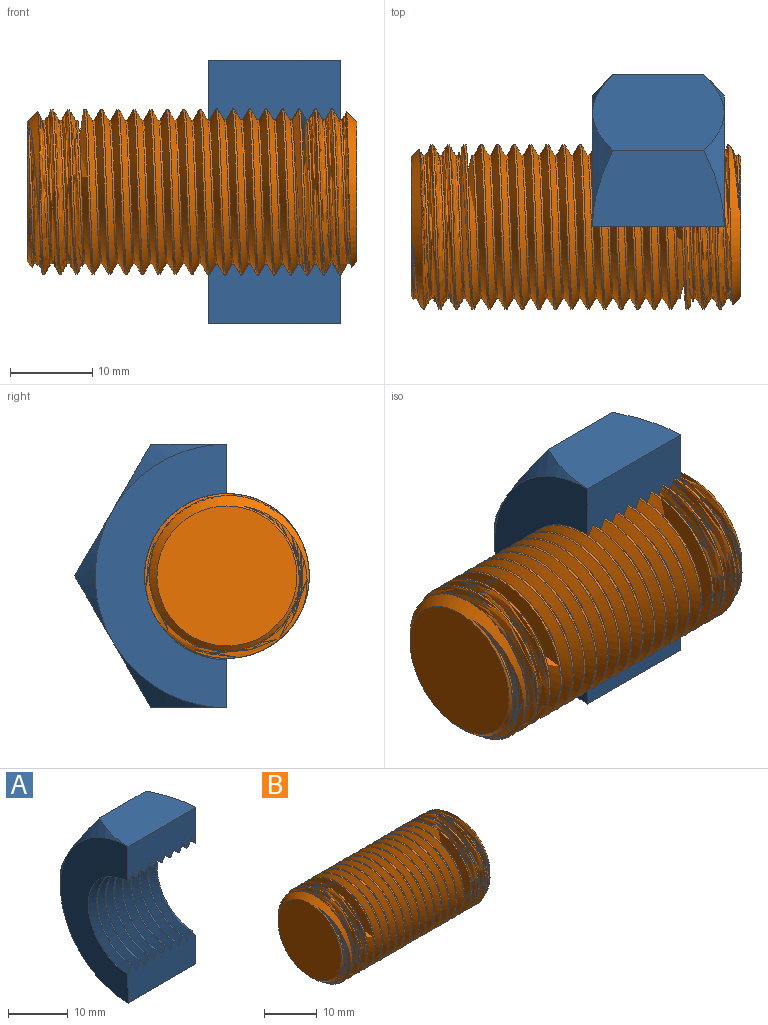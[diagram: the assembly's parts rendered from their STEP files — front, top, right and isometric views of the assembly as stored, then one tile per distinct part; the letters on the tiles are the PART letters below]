
ASSEMBLY  parts=2 mates=1
PART A: 49 faces, bbox 18.7x28.2x37.9 mm
  f0: plane 16x7.23mm, normal (0,-1,0), area 105.3mm2, adj f9,f11,f12,f13,f14,f15,f16,f17
  f1: cone r=18.5mm half-angle=45deg, axis (-1,0,0), area 19.5mm2, adj f2,f4,f47
  f2: plane 16.01x16mm, normal (0,0.87,-0.5), area 264.2mm2, adj f1,f3,f4,f6,f7,f8
  f3: cone r=18.5mm half-angle=45deg, axis (-1,0,0), area 19.5mm2, adj f2,f6,f47
  f4: plane 16.01x16mm, normal (0,0.87,0.5), area 264.2mm2, adj f1,f2,f5,f8,f9,f10
  f5: cone r=18.5mm half-angle=45deg, axis (-1,0,0), area 19.5mm2, adj f4,f9,f47
  f6: plane 16.01x9.24mm, normal (0,0,-1), area 132.1mm2, adj f2,f3,f7,f48
  f7: cone r=18.5mm half-angle=45deg, axis (1,0,0), area 19.5mm2, adj f2,f6,f46
  f8: cone r=18.5mm half-angle=45deg, axis (1,0,0), area 19.5mm2, adj f2,f4,f46
  f9: plane 16.01x9.24mm, normal (0,0,1), area 132.1mm2, adj f0,f4,f5,f10
  f10: cone r=18.5mm half-angle=45deg, axis (1,0,0), area 19.5mm2, adj f4,f9,f46
  f11: cylinder r=8.77mm len=17.53mm, axis (-1,0,0), area 7.2mm2, adj f0,f12,f19,f48
  f12: bspline ~20.54x20.33mm, area 48.1mm2, adj f0,f11,f13,f48
  f13: cylinder r=10.17mm len=20.33mm, axis (-1,0,0), area 3.9mm2, adj f0,f12,f15,f46,f48
  f14: cylinder r=8.77mm len=3.52mm, axis (-1,0,0), area 0.2mm2, adj f0,f15,f46
  f15: bspline ~20.54x20.33mm, area 26.1mm2, adj f0,f13,f14,f46
  f16: cylinder r=8.77mm len=17.53mm, axis (-1,0,0), area 7.2mm2, adj f0,f17,f23,f48
  f17: bspline ~20.54x20.33mm, area 48.1mm2, adj f0,f16,f18,f48
  f18: cylinder r=10.17mm len=20.33mm, axis (-1,0,0), area 4mm2, adj f0,f17,f19,f48
  f19: bspline ~20.54x20.33mm, area 48.1mm2, adj f0,f11,f18,f48
  f20: cylinder r=8.77mm len=17.53mm, axis (-1,0,0), area 7.2mm2, adj f0,f21,f27,f48
  f21: bspline ~20.54x20.33mm, area 48.1mm2, adj f0,f20,f22,f48
  f22: cylinder r=10.17mm len=20.33mm, axis (-1,0,0), area 4mm2, adj f0,f21,f23,f48
  f23: bspline ~20.54x20.33mm, area 48.1mm2, adj f0,f16,f22,f48
  f24: cylinder r=8.77mm len=17.53mm, axis (-1,0,0), area 7.2mm2, adj f0,f25,f31,f48
  f25: bspline ~20.54x20.33mm, area 48.1mm2, adj f0,f24,f26,f48
  f26: cylinder r=10.17mm len=20.33mm, axis (-1,0,0), area 4mm2, adj f0,f25,f27,f48
  f27: bspline ~20.54x20.33mm, area 48.1mm2, adj f0,f20,f26,f48
  f28: cylinder r=8.77mm len=17.53mm, axis (-1,0,0), area 7.2mm2, adj f0,f29,f35,f48
  f29: bspline ~20.54x20.33mm, area 48.1mm2, adj f0,f28,f30,f48
  f30: cylinder r=10.17mm len=20.33mm, axis (-1,0,0), area 4mm2, adj f0,f29,f31,f48
  f31: bspline ~20.54x20.33mm, area 48.1mm2, adj f0,f24,f30,f48
  f32: cylinder r=8.77mm len=17.53mm, axis (-1,0,0), area 7.2mm2, adj f0,f33,f39,f48
  f33: bspline ~20.54x20.33mm, area 48.1mm2, adj f0,f32,f34,f48
  f34: cylinder r=10.17mm len=20.33mm, axis (-1,0,0), area 4mm2, adj f0,f33,f35,f48
  f35: bspline ~20.54x20.33mm, area 48.1mm2, adj f0,f28,f34,f48
  f36: cylinder r=8.77mm len=17.53mm, axis (-1,0,0), area 7.2mm2, adj f0,f37,f43,f48
  f37: bspline ~20.54x20.33mm, area 48.1mm2, adj f0,f36,f38,f48
  f38: cylinder r=10.17mm len=20.33mm, axis (-1,0,0), area 4mm2, adj f0,f37,f39,f48
  f39: bspline ~20.54x20.33mm, area 48.1mm2, adj f0,f32,f38,f48
  f40: cylinder r=8.77mm len=17.53mm, axis (-1,0,0), area 6.9mm2, adj f0,f41,f45,f47,f48
  f41: bspline ~20.54x20.33mm, area 48.1mm2, adj f0,f40,f42,f48
  f42: cylinder r=10.17mm len=20.33mm, axis (-1,0,0), area 4mm2, adj f0,f41,f43,f48
  f43: bspline ~20.54x20.33mm, area 48.1mm2, adj f0,f36,f42,f48
  f44: cylinder r=10.17mm len=2.08mm, axis (-1,0,0), area 0.1mm2, adj f45,f47,f48
  f45: bspline ~20.33x11.74mm, area 22mm2, adj f40,f44,f47,f48
  f46: plane 32.92x16.92mm, normal (-1,0,0), area 262.4mm2, adj f0,f7,f8,f10,f13,f14,f15,f48
  f47: plane 32.92x16.92mm, normal (1,0,0), area 262.4mm2, adj f0,f1,f3,f5,f40,f44,f45,f48
  f48: plane 16x7.23mm, normal (0,-1,0), area 105.3mm2, adj f6,f11,f12,f13,f16,f17,f18,f19
PART B: 8 faces, bbox 41.8x23.1x20 mm
  f0: plane 17x17mm, normal (1,0,0), area 227mm2, adj f3
  f1: cylinder r=10mm len=37mm, axis (-1,0,0), area 568.4mm2, adj f3,f4,f5,f7
  f2: plane 17x17mm, normal (-1,0,0), area 227mm2, adj f4
  f3: cone r=10mm half-angle=45deg, axis (-1,0,0), area 68.4mm2, adj f0,f1,f5,f6,f7
  f4: cone r=8.5mm half-angle=45deg, axis (1,0,0), area 68.4mm2, adj f1,f2,f5,f6,f7
  f5: bspline ~40.75x23.09mm, area 1706.6mm2, adj f1,f3,f4,f6
  f6: cylinder r=8.7mm len=39.6mm, axis (-1,0,0), area 259.2mm2, adj f3,f4,f5,f7
  f7: bspline ~40.75x23.09mm, area 1686.1mm2, adj f1,f3,f4,f6
PLACE A t=(0.56,-3.23,6.79)mm
PLACE B t=(-9.44,-3.23,6.79)mm fixed
MATE cylindrical A.f1 <-> B.f1  axis (1,0,0) through (8.56,-3.23,6.79)mm
